# Revit family: PRD_AR_ShwrThrmsttcVlvs_ThermostaticSingle-leverIn-wallMixer_F5LT2005
name_source: partatom
category: Plumbing Fixtures
units: mm (PartAtom-declared; Revit-internal decimal feet)

## family parameters
Cut with Voids When Loaded = Yes
Host = Face
OmniClass Number = 23.65.55.14.24
OmniClass Title = Mixing Valves for Liquid Services
Part Type = Normal
Room Calculation Point = No
Round Connector Dimension = Use Diameter
Shared = No

## types (1)
- F5LT2005
    AccentColour = chrome-look (glossy
    AdditionalConnections = no
    AssetType = Fixed
    BIMObjectName = PRD_AR_ShowerThermostaticValves_ThermostaticSingle-leverIn-wallMixer_F5LT2005
    BasicColour = stainless steel-look
    BodyMaterial = PRD_AR_ChromatedBrass_HighPolished
    Built-inFittingModel = Finishing section
    Category = Pr_40_20_87_80, Shower thermostatic valves
    Circulation = no
    CloseOffRating = 0.0 Pa
    Color = stainless steel
    ConnectionWithPayWaterDispenser = not possible
    CoverplateHeight = 245 mm
    CoverplateWidth = 190 mm
    Default Elevation = 1219 mm
    Description = F5L-Therm thermostatic single-lever mixer DN 15 as finished installation kit for in-wall installation in basic installation kit, for shower facilities. For connection to hot and cold water. Function block with integrated thermostatic cartridge and mechanism for an optional hygiene unit for automatic hygiene flushing, program-controlled thermal disinfection (additional bypass solenoid valve cartridge necessary) and storage of statistical data.Thermostatically-controlled mixer cartridge with expansion element and active scald protection as well as adjustable and turn-proof temperature stop, and ceramic disc technology. All-metal construction, visible parts high-polished, chrome-plated. Holding frame including profile seal, stainless-steel cover plate 190 x 245mm with covered screw fixing, chrome-plated plastic rosette, backflow preventer and strainers. Depth adjustability 25 mm.
    DiameterNominal = 15  [stored 0.0492126 ft]
    DurationUnit = year
    Features = For connection to hot water and cold water. Depth adjustability 25 mm.
    Finish = polished chrome-plated
    FlowCoefficient = 0
    ForHandShower = no
    FunctionalPrinciple = manual
    HygieneFlushing = prepared
    IfcExportAs = IfcValveType
    IfcExportType = MIXING
    InletSize = G 3/4 B
    LockingMechanism = Top section, ceramic
    Manufacturer = KWC Group AG
    ManufacturerName = KWC Group AG
    ManufacturerURL = www.kwc.com
    Material = Brass
    MaterialCasing = stainless steel
    MaterialFitting = brass-look
    MinimumFlowPressure = 1 bar
    MixerControl = THERMOSTATIC
    Model = F5LT2005
    ModelNumber = 2030066500
    ModelReference = F5LT2005
    NBSDescription = Shower mixers
    NBSReference = 45-35-70/335
    Name = F5L-Therm thermostatic single-lever in-wall mixer F5LT2005
    NominalDepth = 0 mm  [stored 0 ft]
    NominalHeight = 245 mm  [stored 0.803806 ft]
    NominalWidth = 190 mm  [stored 0.62336 ft]
    OutletConnectionSize = 15 mm  [stored 0.0492126 ft]
    PositionOfWaterConnection = from side
    ProductInformation = http://pim.kwc.com
    ProtectiveShutdown = no
    ShowerPipeDraining = no
    Size = 15
    SoundInsulation = no
    Status = New
    SurfaceFinishCasing = satin finished
    SurfaceFinishFitting = chromed
    SurfaceTreatmentFitting = polished
    TailorMade = no
    TemperatureLimit = yes
    TestPressure = 0.0 Pa
    ThermalDisinfection = yes
    TypeOfMixing = with thermostat
    TypeOfMounting = in-wall installation with box
    TypeOfOperation = manual operation
    TypeOfShower = in-wall fitting
    URL = www.kwc.com
    Uniclass2015Code = Pr_40_20_87_80
    Uniclass2015Title = Shower thermostatic valves
    Uniclass2015Version = Products v1.32
    ValveMechanism = OTHER
    ValveOperation = OTHER
    ValvePattern = ANGLED_2_PORT
    Version = 1
    VolumeFlowRate = 0.23 l/s at 3 bar
    WarrantyDurationUnit = year
    WaterConnection = threaded connection (external)
    WithBackflowPreventer = yes
    WithFilter = yes
    WithRosettesOrCoverPlate = yes
    WithTransformerOrPowerSupply = no
    WorkingPressure = 0.0 Pa

note: [stored X ft] marks values corroborated as IEEE doubles in the binary element streams (Revit-internal decimal feet)

## geometry (parser evidence)
native form markers: Sweep x8
no freeform markers — native parametric forms only
